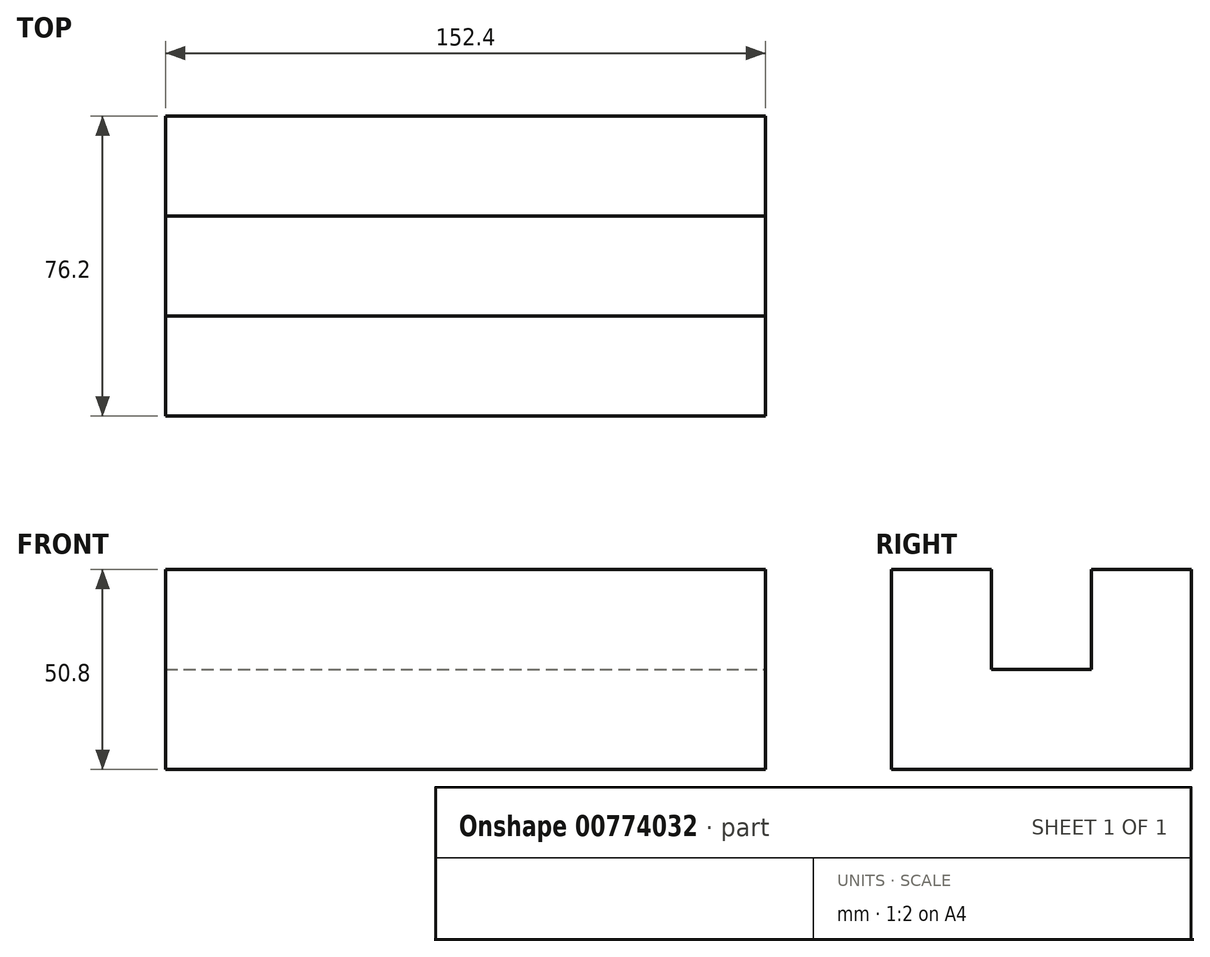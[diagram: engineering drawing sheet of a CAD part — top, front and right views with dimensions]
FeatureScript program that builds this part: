
annotation { "Feature Type Name" : "Feature", "Feature Type Description" : "" }
export const myFeature = defineFeature(function(context is Context, id is Id, definition is map)
    precondition{}
    {
        {
            var Q0;
            Q0=qCreatedBy(makeId("Front.planeOp"),FACE);
            var sketch = newSketch(context, id + "F0", { "sketchPlane" : qUnion([Q0])});
            skLineSegment(sketch, "E0", {"start": v(0, 0) * mm, "end": v(152.4, 0) * mm});
            skLineSegment(sketch, "E1", {"start": v(152.4, 0) * mm, "end": v(152.4, 50.8) * mm});
            skLineSegment(sketch, "E2", {"start": v(152.4, 50.8) * mm, "end": v(0, 50.8) * mm});
            skLineSegment(sketch, "E3", {"start": v(0, 50.8) * mm, "end": v(0, 0) * mm});
            skSolve(sketch);
        }
        {
            var Q0;
            Q0=makeQuery(id+"F0.imprint","IMPRINT",FACE,{"disambiguationData":[TD([[makeQuery(id+"F0.imprint","IMPRINT",EDGE,{"derivedFrom":sQuery(id+"F0.wireOp",EDGE,"E0")}),1.0]])]});
            extrude(context, id + "F1", {"entities" : qUnion([Q0]), "depth" : 76.2 * mm, "offsetDistance" : 25.4 * mm});
        }
        {
            var Q0;
            Q0=makeQuery(id+"F1.opExtrude","SWEPT_FACE",FACE,{"disambiguationData":[OSD([sQuery(id+"F0.wireOp",EDGE,"E1")])]});
            var sketch = newSketch(context, id + "F2", { "sketchPlane" : qUnion([Q0])});
            skLineSegment(sketch, "E4", {"start": v(-25.4, 50.8) * mm, "end": v(-25.4, 25.4) * mm});
            skLineSegment(sketch, "E5", {"start": v(-25.4, 25.4) * mm, "end": v(-50.8, 25.4) * mm});
            skLineSegment(sketch, "E6", {"start": v(-50.8, 25.4) * mm, "end": v(-50.8, 50.8) * mm});
            skLineSegment(sketch, "E7", {"start": v(-50.8, 50.8) * mm, "end": v(-25.4, 50.8) * mm});
            skSolve(sketch);
        }
        {
            var Q0;
            Q0=makeQuery(id+"F2.imprint","IMPRINT",FACE,{"disambiguationData":[TD([[makeQuery(id+"F2.imprint","IMPRINT",EDGE,{"derivedFrom":sQuery(id+"F2.wireOp",EDGE,"E4")}),-1.0]])]});
            extrude(context, id + "F3", {"entities" : qUnion([Q0]), "operationType" : NewBodyOperationType.REMOVE, "oppositeDirection" : true, "depth" : 152.4 * mm, "offsetDistance" : 25.4 * mm});
        }
    });
